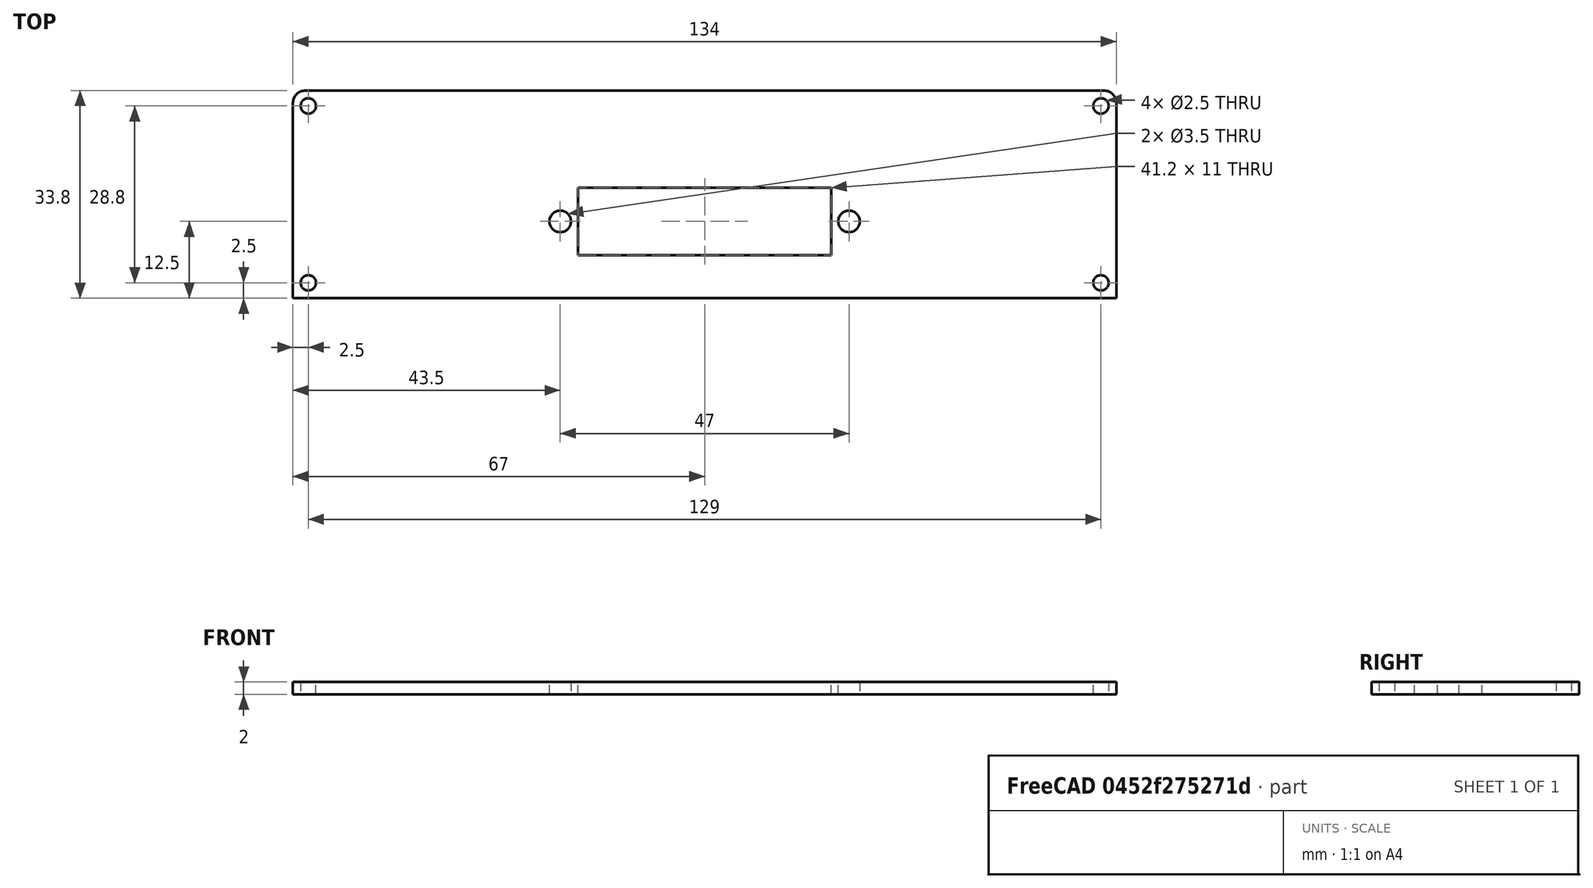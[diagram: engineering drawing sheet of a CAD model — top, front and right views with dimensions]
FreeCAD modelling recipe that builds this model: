
FCSTD DOCUMENT  (FreeCAD 0.19R23141 (Git))
Label: 接线盒前板
License: All rights reserved
LicenseURL: http://en.wikipedia.org/wiki/All_rights_reserved
objects: TechDraw::DrawViewDimension×5, Sketcher::SketchObject×4, PartDesign::Pocket×3, PartDesign::Mirrored×2, PartDesign::Pad×1, PartDesign::Fillet×1, TechDraw::DrawSVGTemplate×1, PartDesign::PolarPattern×1, PartDesign::Body×1, TechDraw::DrawViewPart×1, TechDraw::DrawPage×1
note: 18 computed .brp shape members not serialized (recipe doc carries the construction recipe); baked Part::Feature solids carry a one-line shape summary decoded from their .brp

FEATURE [Sketcher::SketchObject] Sketch
  MapMode = 5
  Support = -> [XY_Plane]
  sketch-geometry (4):
    g0: LineSegment StartX=-67 StartY=16.9 StartZ=0 EndX=67 EndY=16.9 EndZ=0
    g1: LineSegment StartX=67 StartY=16.9 StartZ=0 EndX=67 EndY=-16.9 EndZ=0
    g2: LineSegment StartX=67 StartY=-16.9 StartZ=0 EndX=-67 EndY=-16.9 EndZ=0
    g3: LineSegment StartX=-67 StartY=-16.9 StartZ=0 EndX=-67 EndY=16.9 EndZ=0
  constraints (11):
    c: Coincident(g0,g1)
    c: Coincident(g1,g2)
    c: Coincident(g2,g3)
    c: Coincident(g3,g0)
    c: Horizontal(g0)
    c: Horizontal(g2)
    c: Vertical(g1)
    c: Vertical(g3)
    c: DistanceY(g1,g1) = 33.8
    c: DistanceX(g2,g2) = 134
    c: Symmetric(g0,g1,g-1)
FEATURE [PartDesign::Pad] Pad
  AllowMultiFace = false
  Direction = (1,1,1)
  Length = 2
  Length2 = 100
  Profile = -> Sketch
  Type = 0
FEATURE [Sketcher::SketchObject] Sketch001
  ExternalGeometry = -> [Pad]
  MapMode = 5
  Placement = pos=(0,0,2) rot=(0,0,1;0rad)
  Support = -> [Pad]
  sketch-geometry (4):
    g0: Circle CenterX=-23.5 CenterY=-4.4 CenterZ=0 NormalX=0 NormalY=0 NormalZ=1 AngleXU=0 Radius=1.75
    g1: Circle CenterX=23.5 CenterY=-4.4 CenterZ=0 NormalX=0 NormalY=0 NormalZ=1 AngleXU=0 Radius=1.75
    g2: LineSegment [constr] StartX=-23.5 StartY=-4.4 StartZ=0 EndX=23.5 EndY=-4.4 EndZ=0
    g3: LineSegment [constr] StartX=23.5 StartY=-4.4 StartZ=0 EndX=23.5 EndY=-16.9 EndZ=0
  constraints (10):
    c: Diameter(g1) = 3.5
    c: Diameter(g0) = 3.5
    c: Coincident(g2,g0)
    c: Coincident(g1,g2)
    c: DistanceX(g2,g2) = 47
    c: Vertical(g3)
    c: PointOnObject(g3,g-3)
    c: DistanceY(g3,g3) = 12.5
    c: Coincident(g3,g1)
    c: Symmetric(g0,g1,g-2)
FEATURE [PartDesign::Pocket] Pocket
  AllowMultiFace = false
  BaseFeature = -> Pad
  Length = 5
  Length2 = 100
  Profile = -> Sketch001
  Type = 1
FEATURE [PartDesign::Fillet] Fillet
  Base = -> Pocket [Edge1,Edge2]
  BaseFeature = -> Pocket
  Radius = 2
  SupportTransform = false
FEATURE [TechDraw::DrawSVGTemplate] Template
  EditableTexts = Designed_by_Name=岳晓凯; FC-Date=2020/11/15; FC-Title=Title; Subtitle=接线盒前板
  Height = 210
  Orientation = 1
  Width = 297
FEATURE [Sketcher::SketchObject] Sketch002
  ExternalGeometry = -> [Fillet]
  MapMode = 5
  Support = -> [XY_Plane]
  sketch-geometry (3):
    g0: Circle CenterX=-64.5 CenterY=-14.4 CenterZ=0 NormalX=0 NormalY=0 NormalZ=1 AngleXU=0 Radius=1.25
    g1: LineSegment [constr] StartX=-64.5 StartY=-14.4 StartZ=0 EndX=-64.5 EndY=-16.9 EndZ=0
    g2: LineSegment [constr] StartX=-64.5 StartY=-14.4 StartZ=0 EndX=-67 EndY=-14.4 EndZ=0
  constraints (9):
    c: Diameter(g0) = 2.5
    c: PointOnObject(g2,g-4)
    c: PointOnObject(g1,g-5)
    c: Coincident(g1,g2)
    c: Coincident(g0,g1)
    c: Horizontal(g2)
    c: Vertical(g1)
    c: DistanceX(g2,g2) = 2.5
    c: DistanceY(g1,g1) = 2.5
FEATURE [PartDesign::Pocket] Pocket001
  AllowMultiFace = false
  BaseFeature = -> Fillet
  Length = 5
  Length2 = 100
  Profile = -> Sketch002
  Reversed = true
  Type = 1
FEATURE [PartDesign::Mirrored] Mirrored
  BaseFeature = -> Pocket001
  MirrorPlane = -> YZ_Plane
  Originals = -> [Pocket001]
FEATURE [PartDesign::Mirrored] Mirrored001
  BaseFeature = -> Mirrored
  MirrorPlane = -> XZ_Plane
  Originals = -> [Pocket001]
FEATURE [PartDesign::PolarPattern] PolarPattern
  Angle = 360
  Axis = -> Sketch002 [N_Axis]
  BaseFeature = -> Mirrored001
  Occurrences = 2
  Originals = -> [Pocket001]
FEATURE [Sketcher::SketchObject] Sketch003
  ExternalGeometry = -> [PolarPattern]
  MapMode = 5
  Placement = pos=(0,0,0) rot=(1,0,0;3.14159rad)
  Support = -> [PolarPattern]
  sketch-geometry (5):
    g0: LineSegment StartX=20.6 StartY=-1.1 StartZ=0 EndX=-20.6 EndY=-1.1 EndZ=0
    g1: LineSegment StartX=-20.6 StartY=-1.1 StartZ=0 EndX=-20.6 EndY=9.9 EndZ=0
    g2: LineSegment StartX=-20.6 StartY=9.9 StartZ=0 EndX=20.6 EndY=9.9 EndZ=0
    g3: LineSegment StartX=20.6 StartY=9.9 StartZ=0 EndX=20.6 EndY=-1.1 EndZ=0
    g4: LineSegment [constr] StartX=-20.6 StartY=9.9 StartZ=0 EndX=-20.6 EndY=16.9 EndZ=0
  constraints (14):
    c: Coincident(g0,g1)
    c: Coincident(g1,g2)
    c: Coincident(g2,g3)
    c: Coincident(g3,g0)
    c: DistanceX(g0,g0) = 41.2
    c: Symmetric(g0,g0,g-2)
    c: DistanceY(g0,g1) = 11
    c: Coincident(g4,g1)
    c: PointOnObject(g4,g-3)
    c: Vertical(g4)
    c: DistanceY(g4,g4) = 7
    c: Vertical(g1)
    c: Vertical(g3)
    c: Horizontal(g2)
FEATURE [PartDesign::Pocket] Pocket002
  BaseFeature = -> PolarPattern
  Length = 5
  Length2 = 100
  Profile = -> Sketch003
  Type = 0
FEATURE [PartDesign::Body] Body
  Group = -> [Sketch,Pad,Sketch001,Pocket,Fillet,Sketch002,Pocket001,Mirrored,Mirrored001,PolarPattern,Sketch003,Pocket002]
  Origin = -> Origin
  Tip = -> Pocket002
FEATURE [TechDraw::DrawViewPart] View
  CoarseView = false
  Direction = (0,0,1)
  Focus = 100
  HardHidden = false
  IsoCount = 0
  IsoHidden = false
  IsoVisible = false
  LockPosition = false
  Perspective = false
  Rotation = 0
  ScaleType = 0
  SeamHidden = false
  SeamVisible = false
  SmoothHidden = false
  SmoothVisible = false
  Source = -> [Body]
  X = 144.027
  XDirection = (1,0,0)
  Y = 141.02
FEATURE [TechDraw::DrawViewDimension] Dimension
  Arbitrary = false
  FormatSpec = ⌀%.2f
  Inverted = false
  LockPosition = false
  MeasureType = 1
  OverTolerance = 0
  References2D = -> [View]
  Rotation = 0
  ScaleType = 0
  TheoreticalExact = false
  Type = 5
  UnderTolerance = 0
  X = 8.68932
  Y = -3.11504
FEATURE [TechDraw::DrawViewDimension] Dimension010
  Arbitrary = false
  FormatSpec = %.2f
  Inverted = false
  LockPosition = false
  MeasureType = 1
  OverTolerance = 0
  References2D = -> [View]
  Rotation = 0
  ScaleType = 0
  TheoreticalExact = false
  Type = 1
  UnderTolerance = 0
  X = -1e-06
  Y = -22.4344
FEATURE [TechDraw::DrawViewDimension] Dimension011
  Arbitrary = false
  FormatSpec = %.2f
  Inverted = false
  LockPosition = false
  MeasureType = 1
  OverTolerance = 0
  References2D = -> [View]
  Rotation = 0
  ScaleType = 0
  TheoreticalExact = false
  Type = 1
  UnderTolerance = 0
  X = 0.327899
  Y = 11.4288
FEATURE [TechDraw::DrawViewDimension] Dimension012
  Arbitrary = false
  FormatSpec = %.2f
  Inverted = false
  LockPosition = false
  MeasureType = 1
  OverTolerance = 0
  References2D = -> [View]
  Rotation = 0
  ScaleType = 0
  TheoreticalExact = false
  Type = 2
  UnderTolerance = 0
  X = 38.1426
  Y = -3.90815
FEATURE [TechDraw::DrawViewDimension] Dimension013
  Arbitrary = false
  FormatSpec = %.2f
  Inverted = false
  LockPosition = false
  MeasureType = 1
  OverTolerance = 0
  References2D = -> [View]
  Rotation = 0
  ScaleType = 0
  TheoreticalExact = false
  Type = 2
  UnderTolerance = 0
  X = -38.5858
  Y = -2.08748
FEATURE [TechDraw::DrawPage] Page
  KeepUpdated = true
  NextBalloonIndex = 1
  ProjectionType = 0
  Template = -> Template
  Views = -> [View,Dimension,Dimension010,Dimension011,Dimension012,Dimension013]
